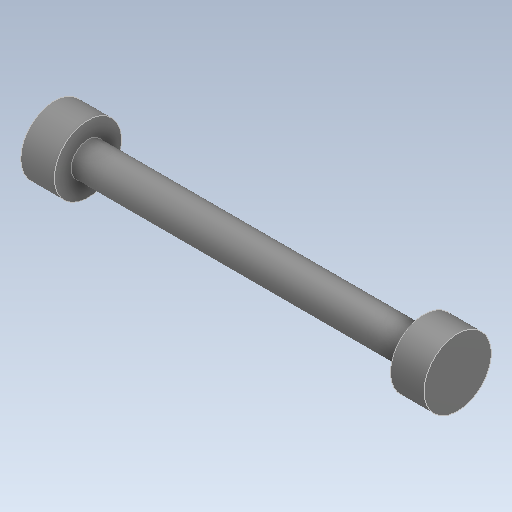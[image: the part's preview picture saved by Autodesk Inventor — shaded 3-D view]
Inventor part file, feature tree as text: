
AUTODESK INVENTOR PART (.ipt)
format: ipt  version: 2021 (Build 250183000, 183)  size: 107,520 bytes
history: mixed  units: mm
features: other x1, revolve x1, imported_body x1
ambient origin geometry x8: Origin, YZ Plane, XZ Plane, XY Plane, X Axis, Y Axis, Z Axis, Center Point
bodies: Body1 (imported_parasolid)
feature tree (3):
  other  "Sólido1"
  revolve  "Revolución1"  [1 undecoded]
  imported_body  NMx_Import_Brep_tag  [imported B-rep: ~7 faces, bbox_mm=[60.0, 0.0, 2.5]]
note: 1 required parameter value undecoded (feature->parameter linkage not recoverable at this tier; creation-order binding heuristic only, values carry confidence <= 0.55)
